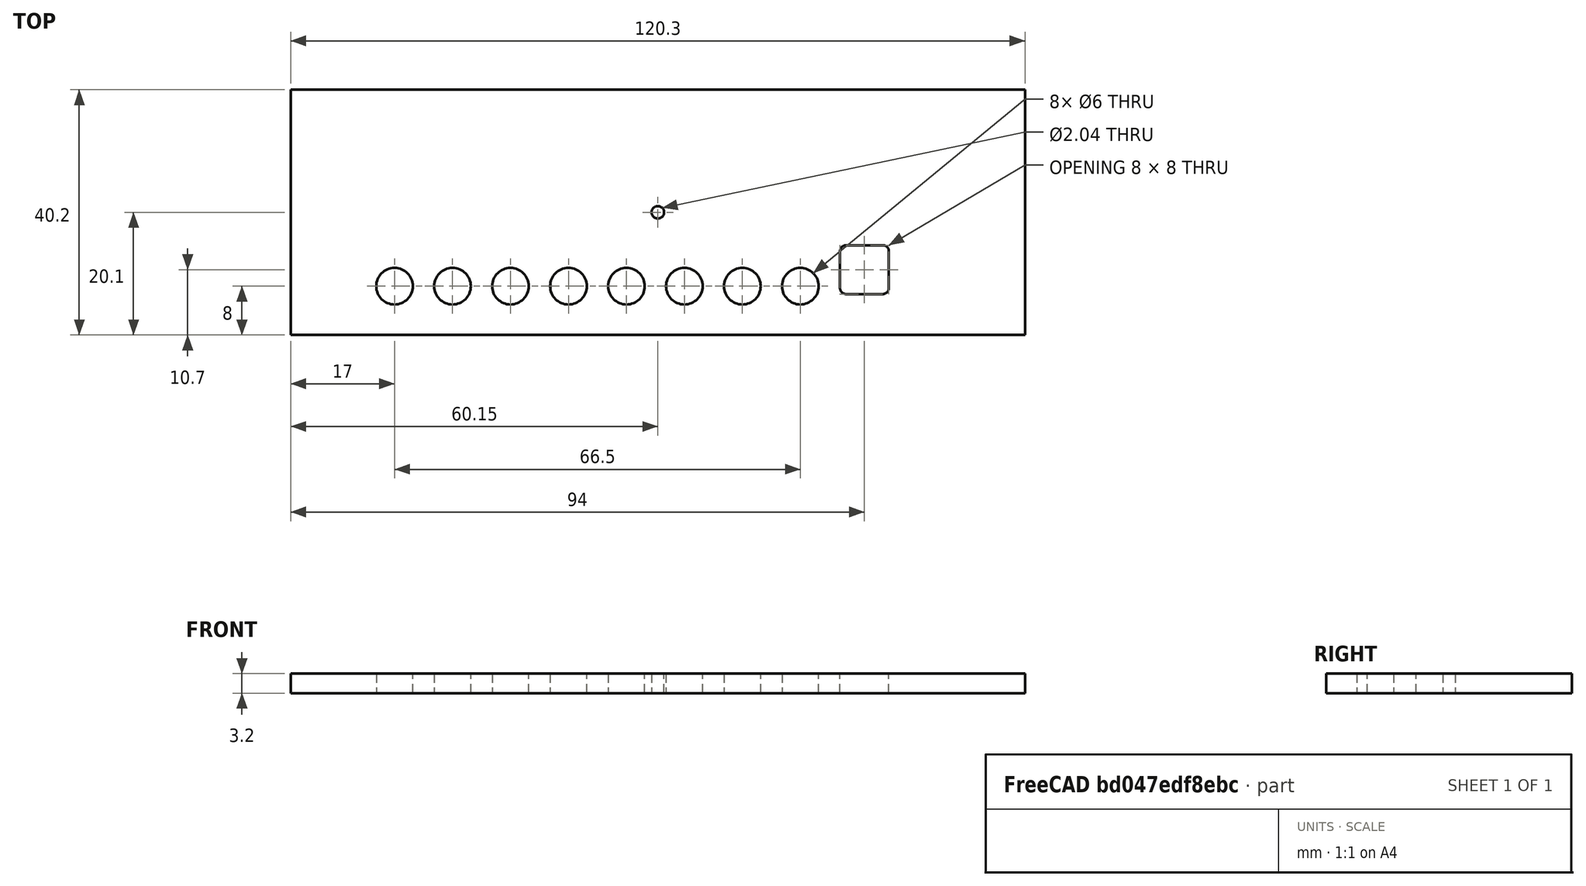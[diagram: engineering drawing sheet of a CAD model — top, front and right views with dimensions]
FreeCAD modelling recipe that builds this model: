
FCSTD DOCUMENT  (FreeCAD 0.21R33694 (Git))
Label: frontside-fc21-2
License: All rights reserved
LicenseURL: http://en.wikipedia.org/wiki/All_rights_reserved
objects: Sketcher::SketchObject×1, PartDesign::Pad×1, PartDesign::Body×1
note: 4 computed .brp shape members not serialized (recipe doc carries the construction recipe); baked Part::Feature solids carry a one-line shape summary decoded from their .brp

FEATURE [Sketcher::SketchObject] Sketch
  FullyConstrained = true
  MapMode = 5
  Support = -> [XY_Plane]
  sketch-geometry (28):
    g0: Circle CenterX=-43.15 CenterY=-12.1 CenterZ=0 NormalX=0 NormalY=0 NormalZ=1 AngleXU=0 Radius=3
    g1: Circle CenterX=-33.65 CenterY=-12.1 CenterZ=0 NormalX=0 NormalY=0 NormalZ=1 AngleXU=0 Radius=3
    g2: Circle CenterX=-24.15 CenterY=-12.1 CenterZ=0 NormalX=0 NormalY=0 NormalZ=1 AngleXU=0 Radius=3
    g3: Circle CenterX=-14.65 CenterY=-12.1 CenterZ=0 NormalX=0 NormalY=0 NormalZ=1 AngleXU=0 Radius=3
    g4: Circle CenterX=13.85 CenterY=-12.1 CenterZ=0 NormalX=0 NormalY=0 NormalZ=1 AngleXU=0 Radius=3
    g5: Circle CenterX=-5.15 CenterY=-12.1 CenterZ=0 NormalX=0 NormalY=0 NormalZ=1 AngleXU=0 Radius=3
    g6: Circle CenterX=4.35 CenterY=-12.1 CenterZ=0 NormalX=0 NormalY=0 NormalZ=1 AngleXU=0 Radius=3
    g7: Circle CenterX=23.35 CenterY=-12.1 CenterZ=0 NormalX=0 NormalY=0 NormalZ=1 AngleXU=0 Radius=3
    g8: LineSegment StartX=-60.15 StartY=20.1 StartZ=0 EndX=60.15 EndY=20.1 EndZ=0
    g9: LineSegment StartX=60.15 StartY=20.1 StartZ=0 EndX=60.15 EndY=-20.1 EndZ=0
    g10: LineSegment StartX=60.15 StartY=-20.1 StartZ=0 EndX=-60.15 EndY=-20.1 EndZ=0
    g11: LineSegment StartX=-60.15 StartY=-20.1 StartZ=0 EndX=-60.15 EndY=20.1 EndZ=0
    g12: LineSegment StartX=36.85 StartY=-5.4 StartZ=0 EndX=30.85 EndY=-5.4 EndZ=0
    g13: LineSegment StartX=29.85 StartY=-6.4 StartZ=0 EndX=29.85 EndY=-12.4 EndZ=0
    g14: LineSegment StartX=30.85 StartY=-13.4 StartZ=0 EndX=36.85 EndY=-13.4 EndZ=0
    g15: LineSegment StartX=37.85 StartY=-12.4 StartZ=0 EndX=37.85 EndY=-6.4 EndZ=0
    g16: ArcOfCircle CenterX=30.85 CenterY=-6.4 CenterZ=0 NormalX=0 NormalY=0 NormalZ=1 AngleXU=0 Radius=1 StartAngle=1.5708 EndAngle=3.14159
    g17: ArcOfCircle CenterX=36.85 CenterY=-6.4 CenterZ=0 NormalX=0 NormalY=0 NormalZ=1 AngleXU=0 Radius=1 StartAngle=0 EndAngle=1.5708
    g18: ArcOfCircle CenterX=36.85 CenterY=-12.4 CenterZ=0 NormalX=0 NormalY=0 NormalZ=1 AngleXU=0 Radius=1 StartAngle=4.71239 EndAngle=6.28319
    g19: ArcOfCircle CenterX=30.85 CenterY=-12.4 CenterZ=0 NormalX=0 NormalY=0 NormalZ=1 AngleXU=0 Radius=1 StartAngle=3.14159 EndAngle=4.71239
    g20: LineSegment StartX=-43.15 StartY=-12.1 StartZ=0 EndX=-33.65 EndY=-12.1 EndZ=0
    g21: LineSegment StartX=-33.65 StartY=-12.1 StartZ=0 EndX=-24.15 EndY=-12.1 EndZ=0
    g22: LineSegment StartX=-24.15 StartY=-12.1 StartZ=0 EndX=-14.65 EndY=-12.1 EndZ=0
    g23: LineSegment StartX=-14.65 StartY=-12.1 StartZ=0 EndX=-5.15 EndY=-12.1 EndZ=0
    g24: LineSegment StartX=-5.15 StartY=-12.1 StartZ=0 EndX=4.35 EndY=-12.1 EndZ=0
    g25: LineSegment StartX=4.35 StartY=-12.1 StartZ=0 EndX=13.85 EndY=-12.1 EndZ=0
    g26: LineSegment StartX=13.85 StartY=-12.1 StartZ=0 EndX=23.35 EndY=-12.1 EndZ=0
    g27: Circle CenterX=0 CenterY=0 CenterZ=0 NormalX=0 NormalY=0 NormalZ=1 AngleXU=0 Radius=1.02
  constraints (70):
    c: Coincident(g8,g9)
    c: Coincident(g9,g10)
    c: Coincident(g10,g11)
    c: Coincident(g11,g8)
    c: Horizontal(g10)
    c: Vertical(g9)
    c: DistanceX(g8,g8) = 120.3
    c: DistanceY(g10,g8) = 40.2
    c: Symmetric(g8,g8,g-2)
    c: Symmetric(g8,g10,g-1)
    c: Equal(g1,g2)
    c: Equal(g2,g3)
    c: Equal(g3,g4)
    c: Equal(g4,g5)
    c: Equal(g5,g6)
    c: Equal(g6,g7)
    c: Horizontal(g12)
    c: Horizontal(g14)
    c: Vertical(g13)
    c: Vertical(g15)
    c: Tangent(g12,g16) = -1.5708
    c: Tangent(g13,g16) = -1.5708
    c: Tangent(g12,g17) = -1.5708
    c: Tangent(g15,g17) = -1.5708
    c: Tangent(g15,g18) = -1.5708
    c: Tangent(g14,g18) = -1.5708
    c: Tangent(g14,g19) = -1.5708
    c: Tangent(g13,g19) = -1.5708
    c: Equal(g1,g0)
    c: Equal(g18,g19)
    c: Equal(g19,g16)
    c: Equal(g16,g17)
    c: Radius(g17) = 1
    c: DistanceX(g10,g0) = 17
    c: DistanceX(g0,g1) = 9.5
    c: DistanceY(g10,g0) = 8
    c: DistanceX(g15,g8) = 22.3
    c: DistanceX(g13,g15) = 8
    c: Radius(g0) = 3
    c: Coincident(g20,g0)
    c: Coincident(g20,g1)
    c: Horizontal(g20)
    c: Coincident(g21,g1)
    c: Coincident(g21,g2)
    c: Horizontal(g21)
    c: Coincident(g22,g2)
    c: Coincident(g22,g3)
    c: Horizontal(g22)
    c: Coincident(g23,g3)
    c: Coincident(g23,g5)
    c: Horizontal(g23)
    c: Coincident(g24,g5)
    c: Coincident(g24,g6)
    c: Horizontal(g24)
    c: Coincident(g25,g6)
    c: Coincident(g25,g4)
    c: Horizontal(g25)
    c: Coincident(g26,g4)
    c: Coincident(g26,g7)
    c: Horizontal(g26)
    c: Equal(g20,g21)
    c: Equal(g21,g22)
    c: Equal(g22,g23)
    c: Equal(g23,g24)
    c: Equal(g24,g25)
    c: Equal(g25,g26)
    c: DistanceY(g14,g12) = 8
    c: DistanceY(g12,g8) = 25.5
    c: Coincident(g27,g-1)
    c: Radius(g27) = 1.02
FEATURE [PartDesign::Pad] Pad
  Direction = (0,0,1)
  Length = 3.2
  Length2 = 10
  Profile = -> Sketch
  ReferenceAxis = -> Sketch [N_Axis]
  Type = 0
FEATURE [PartDesign::Body] Body
  Group = -> [Sketch,Pad]
  Origin = -> Origin
  Tip = -> Pad
